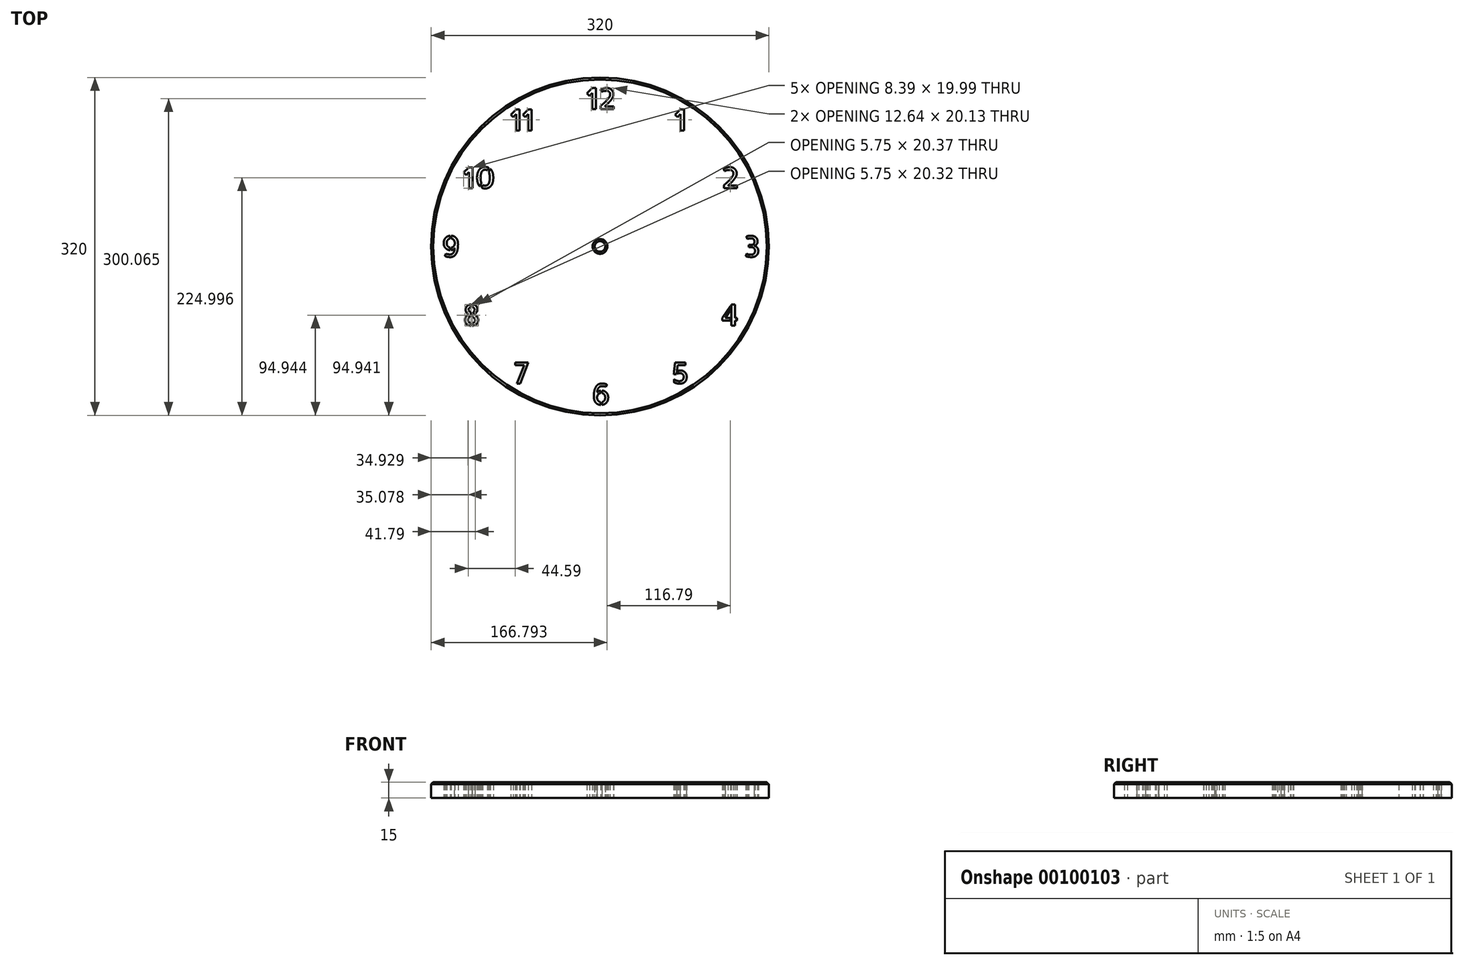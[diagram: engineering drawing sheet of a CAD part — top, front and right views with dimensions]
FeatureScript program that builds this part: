
annotation { "Feature Type Name" : "Feature", "Feature Type Description" : "" }
export const myFeature = defineFeature(function(context is Context, id is Id, definition is map)
    precondition{}
    {
        {
            var Q0;
            Q0=qCreatedBy(makeId("Top.planeOp"),FACE);
            var sketch = newSketch(context, id + "F0", { "sketchPlane" : qUnion([Q0])});
            skLineSegment(sketch, "E0", {"start": v(0, 0) * mm, "end": v(0, -150) * mm, "construction": true});
            skCircle(sketch, "E1.cCircle", {"center": v(0, 0) * mm, "radius": 150 * mm, "construction": true});
            skLineSegment(sketch, "E1.0", {"start": v(0, -150) * mm, "end": v(-75, -129.9) * mm, "construction": true});
            skLineSegment(sketch, "E1.1", {"start": v(-75, -129.9) * mm, "end": v(-129.9, -75) * mm, "construction": true});
            skLineSegment(sketch, "E1.2", {"start": v(-129.9, -75) * mm, "end": v(-150, 0) * mm, "construction": true});
            skLineSegment(sketch, "E1.3", {"start": v(-150, 0) * mm, "end": v(-129.9, 75) * mm, "construction": true});
            skLineSegment(sketch, "E1.4", {"start": v(-129.9, 75) * mm, "end": v(-75, 129.9) * mm, "construction": true});
            skLineSegment(sketch, "E1.5", {"start": v(-75, 129.9) * mm, "end": v(0, 150) * mm, "construction": true});
            skLineSegment(sketch, "E1.6", {"start": v(0, 150) * mm, "end": v(75, 129.9) * mm, "construction": true});
            skLineSegment(sketch, "E1.7", {"start": v(75, 129.9) * mm, "end": v(129.9, 75) * mm, "construction": true});
            skLineSegment(sketch, "E1.8", {"start": v(129.9, 75) * mm, "end": v(150, 0) * mm, "construction": true});
            skLineSegment(sketch, "E1.9", {"start": v(150, 0) * mm, "end": v(129.9, -75) * mm, "construction": true});
            skLineSegment(sketch, "E1.10", {"start": v(129.9, -75) * mm, "end": v(75, -129.9) * mm, "construction": true});
            skLineSegment(sketch, "E1.11", {"start": v(75, -129.9) * mm, "end": v(0, -150) * mm, "construction": true});
            skCircle(sketch, "E2", {"center": v(0, 0) * mm, "radius": 160 * mm});
            skText(sketch, "E3", { "text": "12", "fontName": "AllertaStencil-Regular.ttf"});
            skText(sketch, "E4", { "text": "11", "fontName": "AllertaStencil-Regular.ttf"});
            skCircle(sketch, "E5", {"center": v(0, 0) * mm, "radius": 5 * mm});
            skText(sketch, "E6", { "text": "3", "fontName": "AllertaStencil-Regular.ttf"});
            skText(sketch, "E7", { "text": "6", "fontName": "AllertaStencil-Regular.ttf"});
            skText(sketch, "E8", { "text": "9", "fontName": "AllertaStencil-Regular.ttf"});
            skText(sketch, "E9", { "text": "5", "fontName": "AllertaStencil-Regular.ttf"});
            skText(sketch, "E10", { "text": "10", "fontName": "AllertaStencil-Regular.ttf"});
            skText(sketch, "E11", { "text": "8", "fontName": "AllertaStencil-Regular.ttf"});
            skText(sketch, "E12", { "text": "4", "fontName": "AllertaStencil-Regular.ttf"});
            skText(sketch, "E13", { "text": "7", "fontName": "AllertaStencil-Regular.ttf"});
            skText(sketch, "E14", { "text": "1", "fontName": "AllertaStencil-Regular.ttf"});
            skText(sketch, "E15", { "text": "2", "fontName": "AllertaStencil-Regular.ttf"});
            const initialGuessF0  = {"E3": [-0.01312, 0.13, 1, 0, 0.02], "E4": [-0.08531, 0.1099, 1, 0, 0.02], "E6": [0.1362, -0.01, 1, 0, 0.02], "E7": [-0.0078, -0.15, 1, 0, 0.02], "E8": [-0.15, -0.01, 1, 0, 0.02], "E9": [0.06784, -0.1299, 1, 0, 0.02], "E10": [-0.1299, 0.055, 1, 0, 0.02], "E11": [-0.1299, -0.075, 1, 0, 0.02], "E12": [0.11482, -0.075, 1, 0, 0.02], "E13": [-0.08214, -0.1299, 1, 0, 0.02], "E14": [0.07041, 0.1099, 1, 0, 0.02], "E15": [0.11512, 0.055, 1, 0, 0.02]};
            skSetInitialGuess(sketch, initialGuessF0);
            skSolve(sketch);
        }
        {
            var Q0;
            Q0=makeQuery(id+"F0.imprint","IMPRINT",FACE,{"disambiguationData":[TD([[makeQuery(id+"F0.imprint","IMPRINT",EDGE,{"derivedFrom":sQuery(id+"F0.wireOp",EDGE,"E2")}),1.0]])]});
            extrude(context, id + "F1", {"entities" : qUnion([Q0]), "depth" : 15 * mm});
        }
        {
            var Q0;
            Q0=makeQuery(id+"F1.opExtrude","CAP_EDGE",EDGE,{"disambiguationData":[OSD([sQuery(id+"F0.wireOp",EDGE,"E2")])],"isStart":false});
            var Q1;
            Q1=makeQuery(id+"F1.opExtrude","CAP_EDGE",EDGE,{"disambiguationData":[OSD([sQuery(id+"F0.wireOp",EDGE,"E5")])],"isStart":false});
            chamfer(context, id + "F2", {"entities" : qUnion([Q0, Q1]), "width" : 2 * mm, "tangentPropagation" : true});
        }
    });
